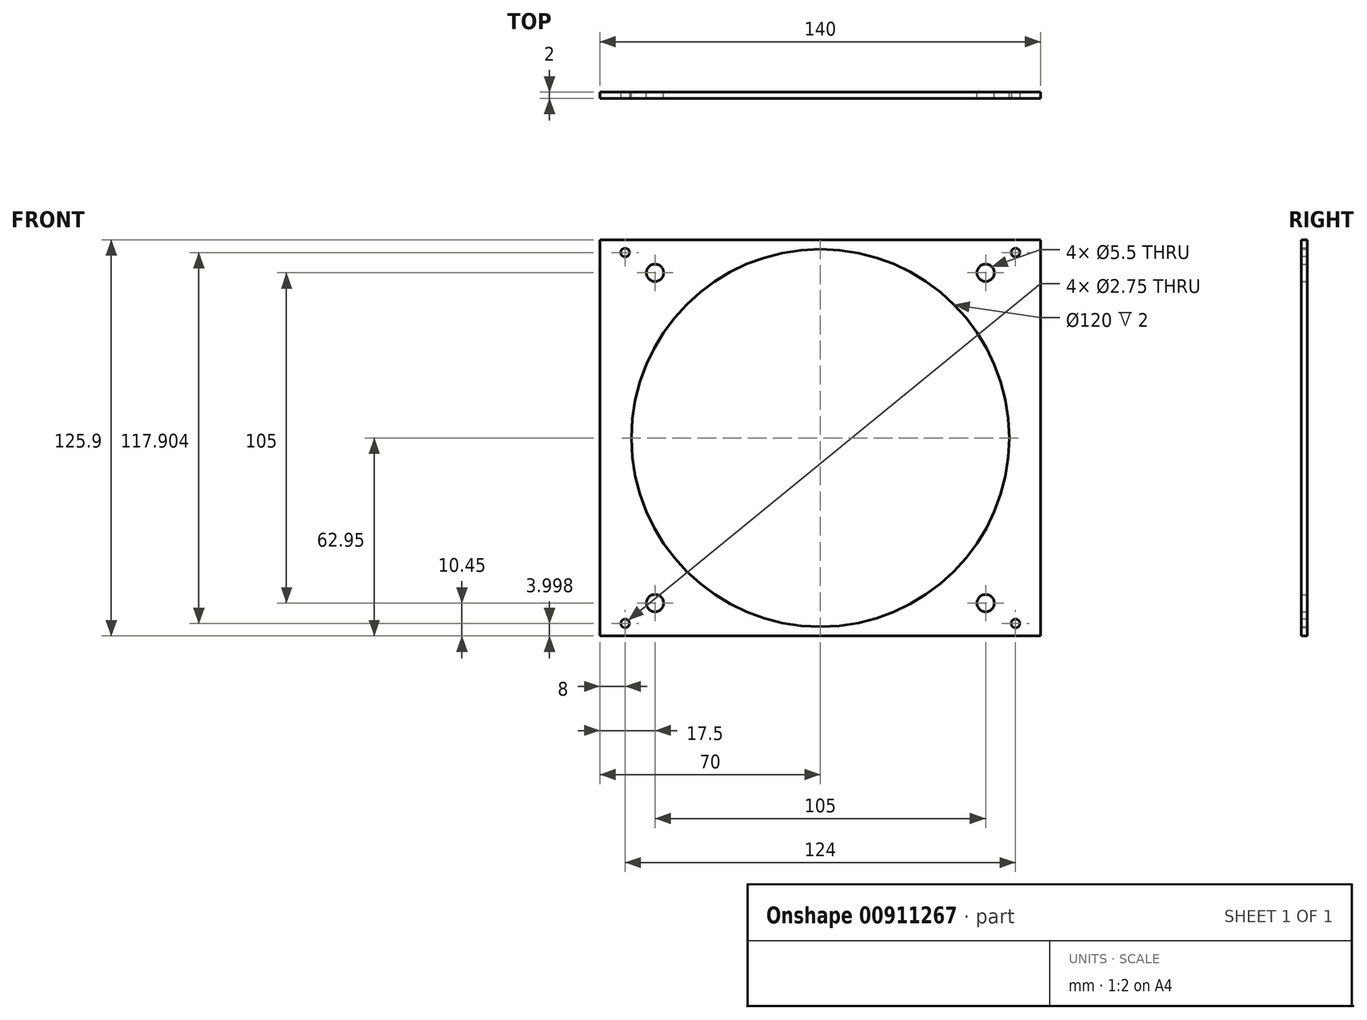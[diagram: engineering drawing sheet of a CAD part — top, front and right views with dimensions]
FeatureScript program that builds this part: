
annotation { "Feature Type Name" : "Feature", "Feature Type Description" : "" }
export const myFeature = defineFeature(function(context is Context, id is Id, definition is map)
    precondition{}
    {
        {
            var Q0;
            Q0=qCreatedBy(makeId("Front.planeOp"),FACE);
            var sketch = newSketch(context, id + "F0", { "sketchPlane" : qUnion([Q0])});
            skLineSegment(sketch, "E0.bottom", {"start": v(52.5, 52.5) * mm, "end": v(-52.5, 52.5) * mm, "construction": true});
            skLineSegment(sketch, "E0.top", {"start": v(52.5, -52.5) * mm, "end": v(-52.5, -52.5) * mm, "construction": true});
            skLineSegment(sketch, "E0.left", {"start": v(52.5, 52.5) * mm, "end": v(52.5, -52.5) * mm, "construction": true});
            skLineSegment(sketch, "E0.right", {"start": v(-52.5, 52.5) * mm, "end": v(-52.5, -52.5) * mm, "construction": true});
            skPoint(sketch, "E0.middle", {"position": v(0, 0) * mm});
            skLineSegment(sketch, "E1.bottom", {"start": v(60, 60) * mm, "end": v(-60, 60) * mm, "construction": true});
            skLineSegment(sketch, "E1.top", {"start": v(60, -60) * mm, "end": v(-60, -60) * mm, "construction": true});
            skLineSegment(sketch, "E1.left", {"start": v(60, 60) * mm, "end": v(60, -60) * mm, "construction": true});
            skLineSegment(sketch, "E1.right", {"start": v(-60, 60) * mm, "end": v(-60, -60) * mm, "construction": true});
            skCircle(sketch, "E2", {"center": v(-52.5, 52.5) * mm, "radius": 2.75 * mm});
            skCircle(sketch, "E3", {"center": v(52.5, 52.5) * mm, "radius": 2.75 * mm});
            skCircle(sketch, "E4", {"center": v(52.5, -52.5) * mm, "radius": 2.75 * mm});
            skCircle(sketch, "E5", {"center": v(-52.5, -52.5) * mm, "radius": 2.75 * mm});
            skLineSegment(sketch, "E6.bottom", {"start": v(-70, 62.95) * mm, "end": v(70, 62.95) * mm});
            skLineSegment(sketch, "E6.top", {"start": v(-70, -62.95) * mm, "end": v(70, -62.95) * mm});
            skLineSegment(sketch, "E6.left", {"start": v(-70, 62.95) * mm, "end": v(-70, -62.95) * mm});
            skLineSegment(sketch, "E6.right", {"start": v(70, 62.95) * mm, "end": v(70, -62.95) * mm});
            skCircle(sketch, "E7", {"center": v(0, 0) * mm, "radius": 60 * mm});
            skSolve(sketch);
        }
        {
            var Q0;
            Q0 = qSketchRegion(id + "F0", true);
            extrude(context, id + "F1", {"entities" : qUnion([Q0]), "endBound" : BoundingType.SYMMETRIC, "depth" : 2 * mm, "offsetDistance" : 25 * mm});
        }
        {
            var Q0;
            Q0=makeQuery(id+"F1.opExtrude","CAP_FACE",FACE,{"disambiguationData":[OSD([sQuery(id+"F0.wireOp",EDGE,"E2"),sQuery(id+"F0.wireOp",EDGE,"E3"),sQuery(id+"F0.wireOp",EDGE,"E4"),sQuery(id+"F0.wireOp",EDGE,"E5"),sQuery(id+"F0.wireOp",EDGE,"E6.bottom"),sQuery(id+"F0.wireOp",EDGE,"E6.top"),sQuery(id+"F0.wireOp",EDGE,"E6.left"),sQuery(id+"F0.wireOp",EDGE,"E6.right"),sQuery(id+"F0.wireOp",EDGE,"E7")])],"isStart":false});
            var sketch = newSketch(context, id + "F2", { "sketchPlane" : qUnion([Q0])});
            skLineSegment(sketch, "E8.bottom", {"start": v(62, 58.95) * mm, "end": v(-62, 58.95) * mm, "construction": true});
            skLineSegment(sketch, "E8.top", {"start": v(62, -58.95) * mm, "end": v(-62, -58.95) * mm, "construction": true});
            skLineSegment(sketch, "E8.left", {"start": v(62, 58.95) * mm, "end": v(62, -58.95) * mm, "construction": true});
            skLineSegment(sketch, "E8.right", {"start": v(-62, 58.95) * mm, "end": v(-62, -58.95) * mm, "construction": true});
            skPoint(sketch, "E8.middle", {"position": v(0, 0) * mm});
            skSolve(sketch);
        }
        {
            var Q0;
            Q0=sQuery(id+"F2.wireOp",VERTEX,"E8.bottom.end");
            var Q1;
            Q1=sQuery(id+"F2.wireOp",VERTEX,"E8.bottom.start");
            var Q2;
            Q2=sQuery(id+"F2.wireOp",VERTEX,"E8.top.start");
            var Q3;
            Q3=sQuery(id+"F2.wireOp",VERTEX,"E8.top.end");
            var Q4;
            Q4=makeQuery(id+"F1.opExtrude","SWEPT_BODY",BODY,{"disambiguationData":[OSD([sQuery(id+"F0.wireOp",EDGE,"E2"),sQuery(id+"F0.wireOp",EDGE,"E3"),sQuery(id+"F0.wireOp",EDGE,"E4"),sQuery(id+"F0.wireOp",EDGE,"E5"),sQuery(id+"F0.wireOp",EDGE,"E6.bottom"),sQuery(id+"F0.wireOp",EDGE,"E6.top"),sQuery(id+"F0.wireOp",EDGE,"E6.left"),sQuery(id+"F0.wireOp",EDGE,"E6.right"),sQuery(id+"F0.wireOp",EDGE,"E7")])]});
            hole(context, id + "F3", {"style" : HoleStyle.SIMPLE, "endStyle" : HoleEndStyle.THROUGH, "holeDiameter" : 2.75 * mm, "majorDiameter" : 5 * mm, "isTappedThrough" : true, "tappedDepth" : 18.5 * mm, "tapClearance" : 3, "locations" : qUnion([Q0, Q1, Q2, Q3]), "scope" : qUnion([Q4])});
        }
    });
